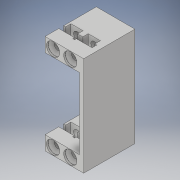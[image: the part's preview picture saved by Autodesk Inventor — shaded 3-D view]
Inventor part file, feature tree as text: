
AUTODESK INVENTOR PART (.ipt)
format: ipt  version: 2020 (Build 240168000, 168)  size: 193,024 bytes
history: native  units: mm
features: other x3, extrude x2, sketch x2, pattern_linear x1
ambient origin geometry x8: Origin, YZ Plane, XZ Plane, XY Plane, X Axis, Y Axis, Z Axis, Center Point
bodies: Solide1 (feature_tree)
feature tree (8):
  other  "base2.ipt"
  pattern_linear  "Réseau rectangulaire1"  Spacing1=10.0mm  [1 undecoded]
  extrude  "Extrusion1"  Depth=20.0mm
  extrude  "Extrusion2"  Depth=2.5mm TaperAngle=0.0deg
  other  "Solide1::base2.ipt"
  other  "FonctionRepérage1"
  sketch  "Esquisse2"
  sketch  "Esquisse3"
note: 1 required parameter value undecoded (feature->parameter linkage not recoverable at this tier; creation-order binding heuristic only, values carry confidence <= 0.55)
